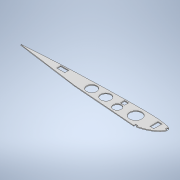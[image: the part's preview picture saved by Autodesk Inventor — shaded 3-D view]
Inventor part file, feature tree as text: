
AUTODESK INVENTOR PART (.ipt)
format: ipt  version: 2021 (Build 250183000, 183)  size: 202,240 bytes
history: native  units: mm
features: extrude x1, sketch x1
ambient origin geometry x8: Origin, YZ Plane, XZ Plane, XY Plane, X Axis, Y Axis, Z Axis, Center Point
bodies: Body1 (feature_tree)
feature tree (2):
  extrude  "Extrusion3"  Depth=20.0mm
  sketch  "Sketch1"  dims[d5=160.0mm d8=160.0mm d10=18.5mm d11=10.0mm d12=20.0mm d13=20.0mm d14=10.0mm d17=5.0mm d18=5.0mm d25=6.0mm d26=5.0mm d27=5.0mm d28=2.0mm d29=0.0mm d30=17.227785mm d31=34.456mm d33=10.0mm d34=10.0mm d35=15.0mm d36=5.0mm d37=5.0mm d41=24.0mm d42=10.0mm d43=10.0mm d47=115.0mm d48=18.5mm d49=104.485399mm d50=368.759386mm d51=30.0mm d52=25.0mm d53=20.0mm d54=25.0mm]
